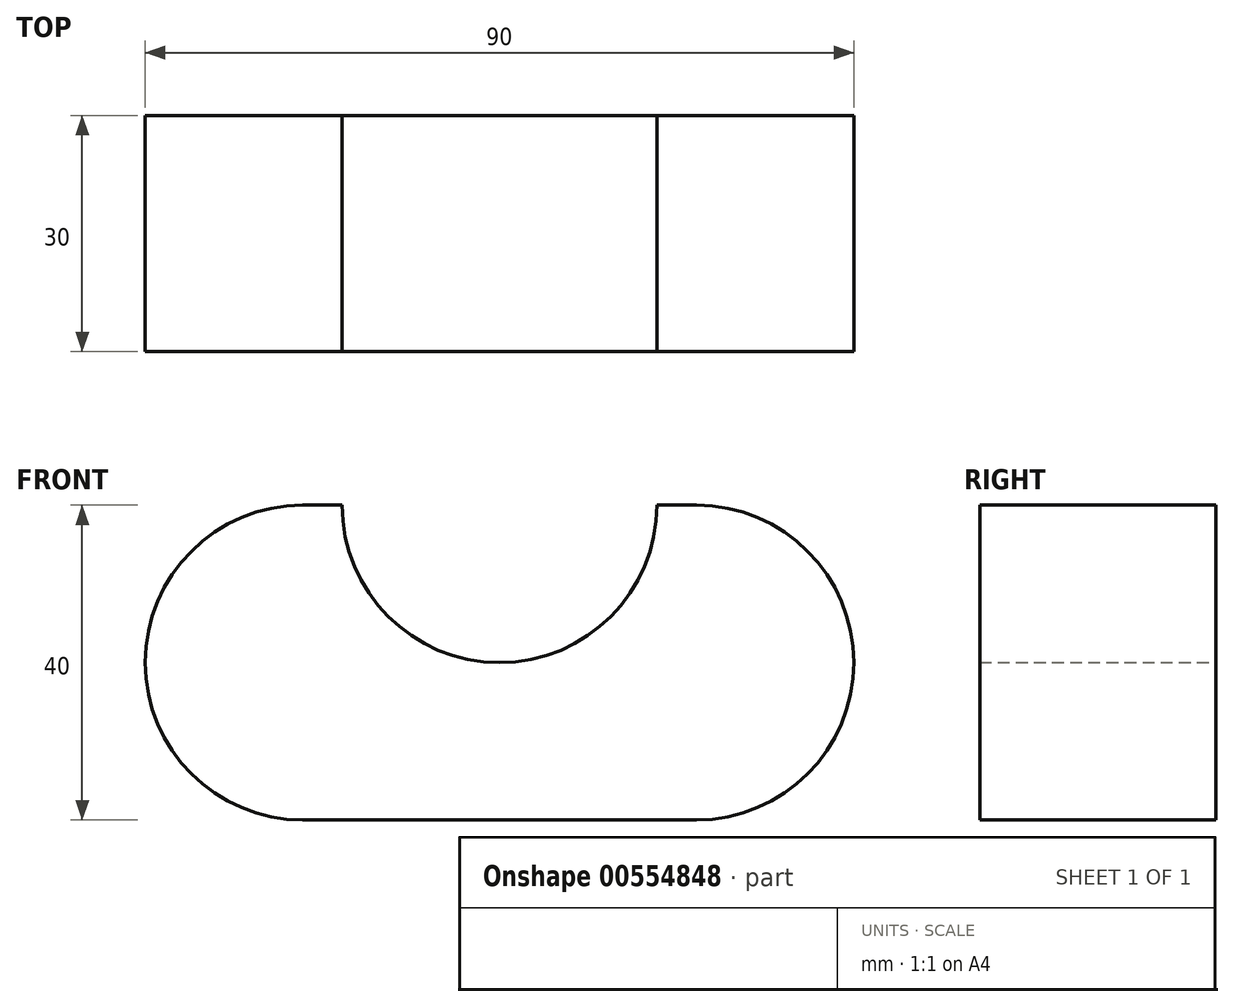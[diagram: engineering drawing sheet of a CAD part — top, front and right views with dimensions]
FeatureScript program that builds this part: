
annotation { "Feature Type Name" : "Feature", "Feature Type Description" : "" }
export const myFeature = defineFeature(function(context is Context, id is Id, definition is map)
    precondition{}
    {
        {
            var Q0;
            Q0=qCreatedBy(makeId("Front.planeOp"),FACE);
            var sketch = newSketch(context, id + "F0", { "sketchPlane" : qUnion([Q0])});
            skLineSegment(sketch, "E0", {"start": v(-63.05, -38.49) * mm, "end": v(-13.05, -38.49) * mm});
            skLineSegment(sketch, "E1", {"start": v(-13.05, 1.51) * mm, "end": v(-18.05, 1.51) * mm});
            skArc(sketch, "E2", {"start": v(-13.05, -38.49) * mm, "mid": v(6.95, -18.49) * mm, "end": v(-13.05, 1.51) * mm});
            skArc(sketch, "E3", {"start": v(-63.05, 1.51) * mm, "mid": v(-83.05, -18.49) * mm, "end": v(-63.05, -38.49) * mm});
            skPoint(sketch, "E4", {"position": v(-38.05, 1.51) * mm});
            skArc(sketch, "E5", {"start": v(-58.05, 1.51) * mm, "mid": v(-38.05, -18.49) * mm, "end": v(-18.05, 1.51) * mm});
            skLineSegment(sketch, "E6.trimOffspring", {"start": v(-58.05, 1.51) * mm, "end": v(-63.05, 1.51) * mm});
            skSolve(sketch);
        }
        {
            var Q0;
            Q0 = qSketchRegion(id + "F0", true);
            extrude(context, id + "F1", {"entities" : qUnion([Q0]), "depth" : 30 * mm, "offsetDistance" : 25 * mm});
        }
    });
